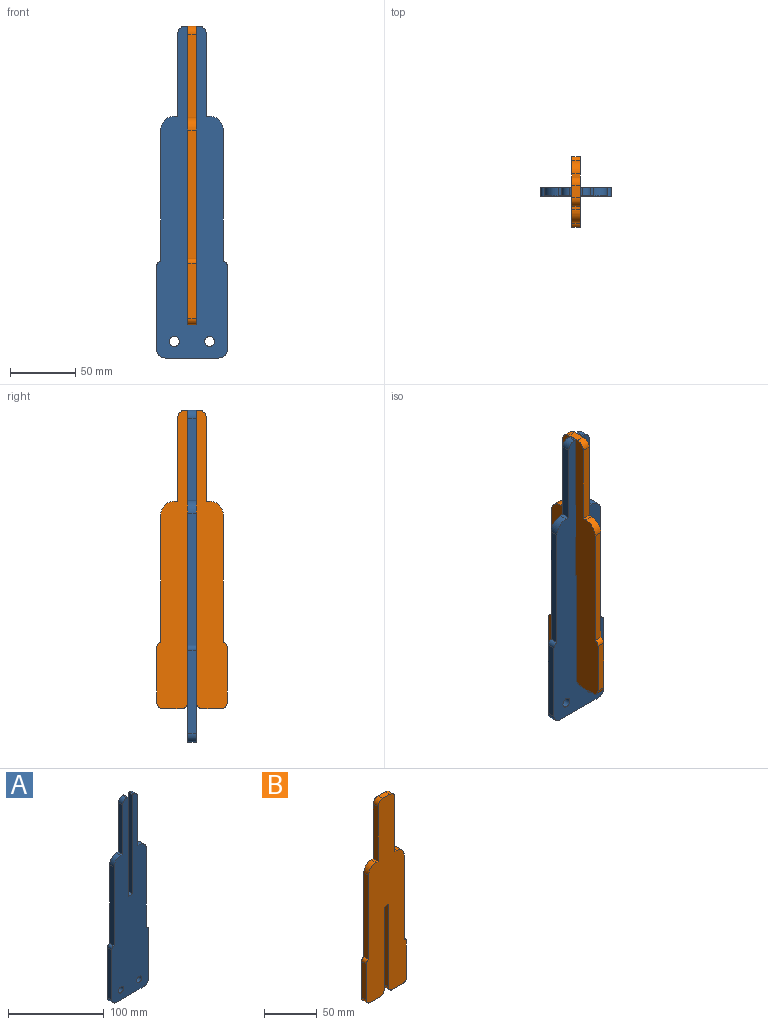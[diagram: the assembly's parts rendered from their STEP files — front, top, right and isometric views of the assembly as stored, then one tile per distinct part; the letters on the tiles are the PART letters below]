
ASSEMBLY  parts=2 mates=1
PART A: 26 faces, bbox 54x6.4x254 mm
  f0: plane 6.35x1.59mm, normal (0,0,1), area 10.1mm2, adj f1,f16,f17,f21
  f1: plane 127x6.35mm, normal (-1,0,0), area 806.5mm2, adj f0,f2,f16,f17
  f2: plane 6.35x6.35mm, normal (0,0,1), area 40.3mm2, adj f1,f3,f16,f17
  f3: plane 127x6.35mm, normal (1,0,0), area 806.5mm2, adj f2,f4,f16,f17
  f4: plane 6.35x1.59mm, normal (0,0,1), area 10.1mm2, adj f3,f16,f17,f20
  f5: plane 62.84x6.35mm, normal (-1,0,0), area 399mm2, adj f6,f16,f17,f20
  f6: plane 6.35x2.54mm, normal (0,0,1), area 16.1mm2, adj f5,f16,f17,f18
  f7: plane 100.54x6.35mm, normal (-1,0,0), area 638.4mm2, adj f16,f17,f18,f22
  f8: plane 64x6.35mm, normal (-1,0,0), area 406.4mm2, adj f16,f17,f22,f24
  f9: plane 41.28x6.35mm, normal (0,0,-1), area 262.1mm2, adj f16,f17,f24,f25
  f10: plane 64x6.35mm, normal (1,0,0), area 406.4mm2, adj f16,f17,f23,f25
  f11: plane 100.54x6.35mm, normal (1,0,0), area 638.4mm2, adj f16,f17,f19,f23
  f12: plane 6.35x2.54mm, normal (0,0,1), area 16.1mm2, adj f15,f16,f17,f19
  f13: cylinder r=3.81mm len=7.62mm, axis (0,1,0), area 152mm2, adj f16,f17
  f14: cylinder r=3.81mm len=7.62mm, axis (0,1,0), area 152mm2, adj f16,f17
  f15: plane 62.84x6.35mm, normal (1,0,0), area 399mm2, adj f12,f16,f17,f21
  f16: plane 254x53.98mm, normal (0,-1,0), area 9827.5mm2, adj f0,f1,f2,f3,f4,f5,f6,f7
  f17: plane 254x53.98mm, normal (0,1,0), area 9827.5mm2, adj f0,f1,f2,f3,f4,f5,f6,f7
  f18: cylinder r=10.16mm len=10.16mm, axis (0,-1,0), area 101.3mm2, adj f6,f7,f16,f17
  f19: cylinder r=10.16mm len=10.16mm, axis (0,1,0), area 101.3mm2, adj f11,f12,f16,f17
  f20: cylinder r=6.35mm len=6.35mm, axis (0,-1,0), area 63.3mm2, adj f4,f5,f16,f17
  f21: cylinder r=6.35mm len=6.35mm, axis (0,1,0), area 63.3mm2, adj f0,f15,f16,f17
  f22: cylinder r=3.81mm len=6.35mm, axis (0,1,0), area 34mm2, adj f7,f8,f16,f17
  f23: cylinder r=3.81mm len=6.35mm, axis (0,1,0), area 34mm2, adj f10,f11,f16,f17
  f24: cylinder r=6.35mm len=6.35mm, axis (0,1,0), area 63.3mm2, adj f8,f9,f16,f17
  f25: cylinder r=6.35mm len=6.35mm, axis (0,-1,0), area 63.3mm2, adj f9,f10,f16,f17
PART B: 26 faces, bbox 54x6.4x228.6 mm
  f0: plane 41.96x6.35mm, normal (1,0,0), area 266.5mm2, adj f14,f15,f20,f25
  f1: plane 97.79x6.35mm, normal (1,0,0), area 621mm2, adj f14,f15,f18,f20
  f2: plane 6.35x2.54mm, normal (0,0,1), area 16.1mm2, adj f3,f14,f15,f18
  f3: plane 63.5x6.35mm, normal (1,0,0), area 403.2mm2, adj f2,f14,f15,f16
  f4: plane 9.53x6.35mm, normal (0,0,1), area 60.5mm2, adj f14,f15,f16,f17
  f5: plane 63.5x6.35mm, normal (-1,0,0), area 403.2mm2, adj f6,f14,f15,f17
  f6: plane 6.35x2.54mm, normal (0,0,1), area 16.1mm2, adj f5,f14,f15,f19
  f7: plane 97.79x6.35mm, normal (-1,0,0), area 621mm2, adj f14,f15,f19,f21
  f8: plane 41.96x6.35mm, normal (-1,0,0), area 266.5mm2, adj f14,f15,f21,f22
  f9: plane 13.65x6.35mm, normal (0,0,-1), area 86.7mm2, adj f14,f15,f22,f23
  f10: plane 96.52x6.35mm, normal (1,0,0), area 612.9mm2, adj f11,f14,f15,f23
  f11: plane 6.35x6.35mm, normal (0,0,-1), area 40.3mm2, adj f10,f12,f14,f15
  f12: plane 96.52x6.35mm, normal (-1,0,0), area 612.9mm2, adj f11,f14,f15,f24
  f13: plane 13.65x6.35mm, normal (0,0,-1), area 86.7mm2, adj f14,f15,f24,f25
  f14: plane 228.6x53.98mm, normal (0,-1,0), area 8700.7mm2, adj f0,f1,f2,f3,f4,f5,f6,f7
  f15: plane 228.6x53.98mm, normal (0,1,0), area 8700.7mm2, adj f0,f1,f2,f3,f4,f5,f6,f7
  f16: cylinder r=6.35mm len=6.35mm, axis (0,1,0), area 63.3mm2, adj f3,f4,f14,f15
  f17: cylinder r=6.35mm len=6.35mm, axis (0,-1,0), area 63.3mm2, adj f4,f5,f14,f15
  f18: cylinder r=10.16mm len=10.16mm, axis (0,1,0), area 101.3mm2, adj f1,f2,f14,f15
  f19: cylinder r=10.16mm len=10.16mm, axis (0,-1,0), area 101.3mm2, adj f6,f7,f14,f15
  f20: cylinder r=3.81mm len=6.35mm, axis (0,1,0), area 34mm2, adj f0,f1,f14,f15
  f21: cylinder r=3.81mm len=6.35mm, axis (0,1,0), area 34mm2, adj f7,f8,f14,f15
  f22: cylinder r=5.08mm len=6.35mm, axis (0,1,0), area 50.7mm2, adj f8,f9,f14,f15
  f23: cylinder r=5.08mm len=6.35mm, axis (0,-1,0), area 50.7mm2, adj f9,f10,f14,f15
  f24: cylinder r=5.08mm len=6.35mm, axis (0,-1,0), area 50.7mm2, adj f12,f13,f14,f15
  f25: cylinder r=5.08mm len=6.35mm, axis (0,-1,0), area 50.7mm2, adj f0,f13,f14,f15
PLACE A t=(9.02,18.8,12.74)mm fixed
PLACE B rot(axis=(0,0,1),90deg) t=(-16.28,44.1,10.2)mm
MATE planar A.f2 <-> B.f11  axis (0,0,1) through (-16.28,18.8,42.3)mm
